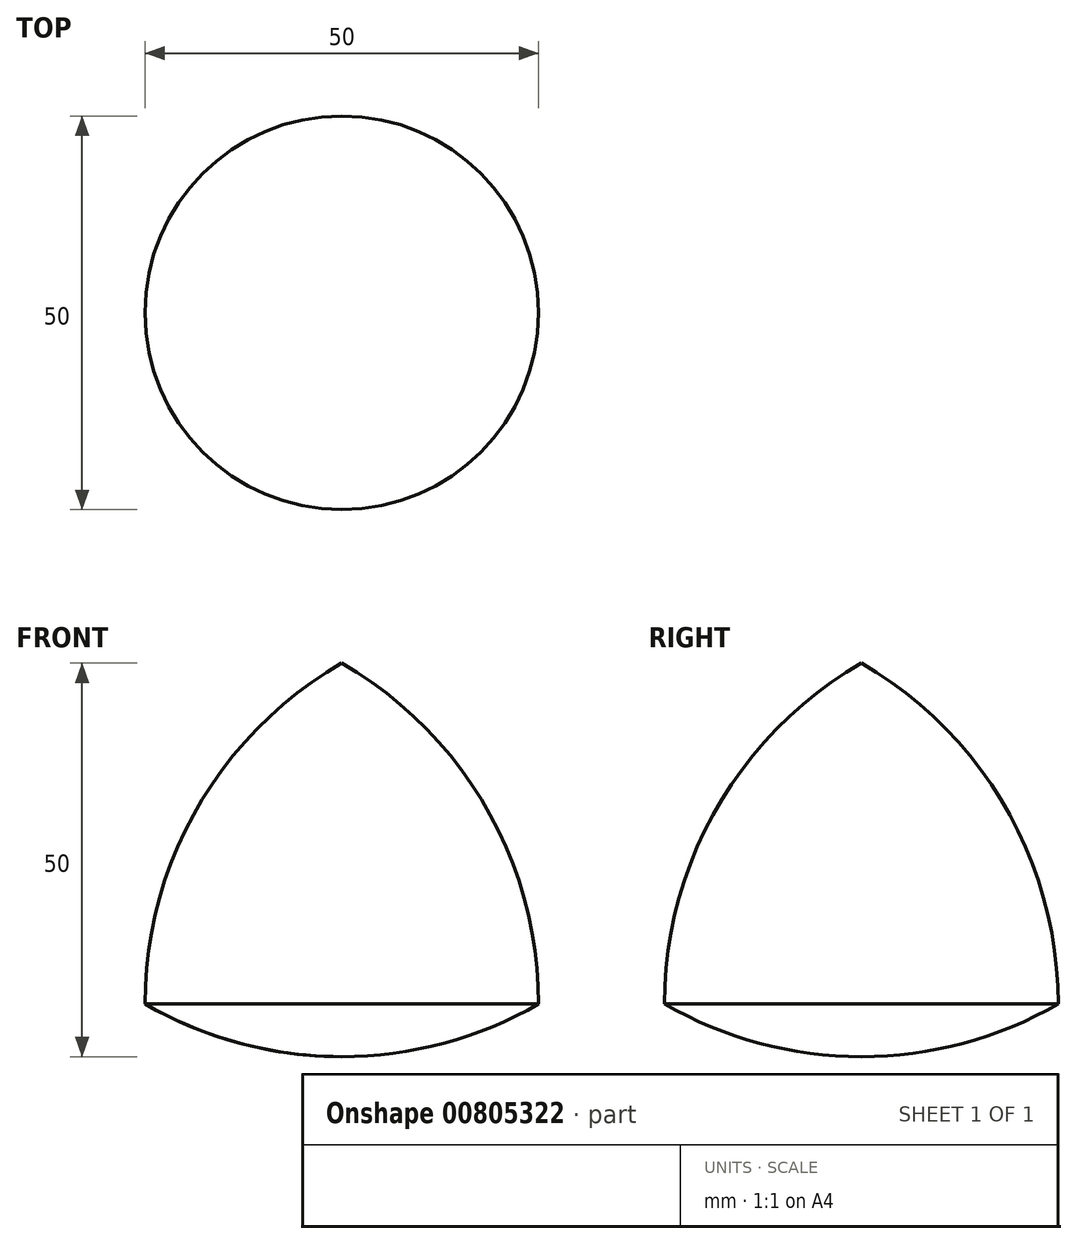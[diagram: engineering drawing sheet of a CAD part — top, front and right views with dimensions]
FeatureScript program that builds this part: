
annotation { "Feature Type Name" : "Feature", "Feature Type Description" : "" }
export const myFeature = defineFeature(function(context is Context, id is Id, definition is map)
    precondition{}
    {
        {
            var Q0;
            Q0=qCreatedBy(makeId("Front.planeOp"),FACE);
            var sketch = newSketch(context, id + "F0", { "sketchPlane" : qUnion([Q0])});
            skCircle(sketch, "E0.cCircle", {"center": v(0, 0) * mm, "radius": 14.43 * mm, "construction": true});
            skLineSegment(sketch, "E0.0", {"start": v(25, -14.43) * mm, "end": v(-25, -14.43) * mm});
            skLineSegment(sketch, "E0.1", {"start": v(-25, -14.43) * mm, "end": v(0, 28.87) * mm});
            skLineSegment(sketch, "E0.2", {"start": v(0, 28.87) * mm, "end": v(25, -14.43) * mm});
            skPoint(sketch, "E0.0.midPoint", {"position": v(0, -14.43) * mm});
            skCircle(sketch, "E1", {"center": v(0, 28.87) * mm, "radius": 50 * mm});
            skCircle(sketch, "E2", {"center": v(25, -14.43) * mm, "radius": 50 * mm});
            skCircle(sketch, "E3", {"center": v(-25, -14.43) * mm, "radius": 50 * mm});
            skLineSegment(sketch, "E4", {"start": v(0, 48.44) * mm, "end": v(0, -40.84) * mm});
            skSolve(sketch);
        }
        {
            var Q0;
            {var subQ0=sQuery(id+"F0.wireOp",EDGE,"E0.2");Q0=makeQuery(id+"F0.imprint","IMPRINT",FACE,{"disambiguationData":[TD([[makeQuery(id+"F0.imprint","IMPRINT",EDGE,{"derivedFrom":subQ0}),1.0]])]});}
            var Q1;
            {var subQ0=sQuery(id+"F0.wireOp",EDGE,"E1");var subQ3=sQuery(id+"F0.wireOp",EDGE,"E4");var subQ5=makeQuery(id+"F0.imprint","INTERSECT",VERTEX,{"derivedFrom":[subQ0,subQ3]});Q1=makeQuery(id+"F0.imprint","IMPRINT",FACE,{"disambiguationData":[TD([[makeQuery(id+"F0.imprint","IMPRINT",EDGE,{"disambiguationData":[TD([[subQ5,1.0]])],"derivedFrom":subQ3}),1.0]])]});}
            var Q2;
            {var subQ1=sQuery(id+"F0.wireOp",EDGE,"E0.2");Q2=makeQuery(id+"F0.imprint","IMPRINT",FACE,{"disambiguationData":[TD([[makeQuery(id+"F0.imprint","IMPRINT",EDGE,{"derivedFrom":subQ1}),-1.0]])]});}
            var Q3;
            Q3=sQuery(id+"F0.wireOp",EDGE,"E4");
            revolve(context, id + "F1", {"surfaceOperationType" : NewSurfaceOperationType.NEW, "entities" : qUnion([Q0, Q1, Q2]), "axis" : qUnion([Q3]), "revolveType" : RevolveType.FULL});
        }
    });
